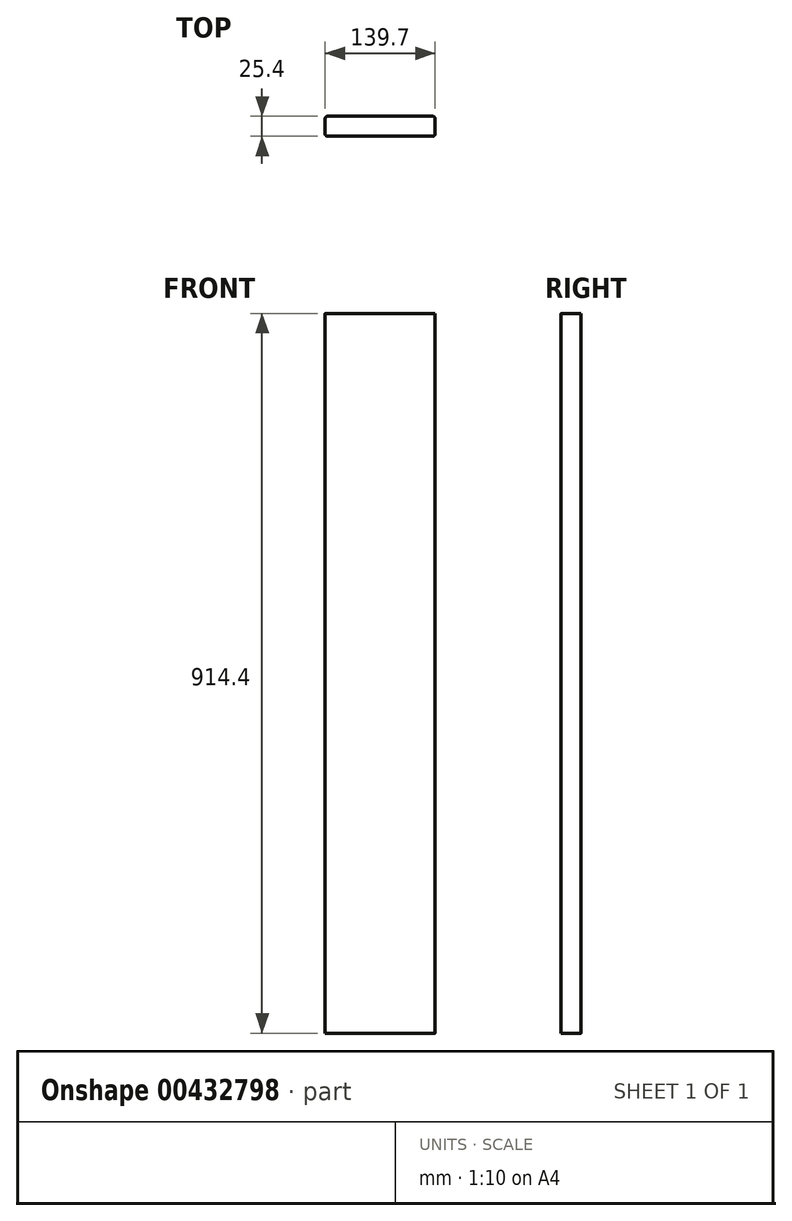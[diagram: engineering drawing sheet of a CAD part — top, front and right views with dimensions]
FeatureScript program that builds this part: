
annotation { "Feature Type Name" : "Feature", "Feature Type Description" : "" }
export const myFeature = defineFeature(function(context is Context, id is Id, definition is map)
    precondition{}
    {
        {
            assignVariable(context, id + "F0", {"name" : "Length", "anyValue" : 914.4 * mm});
        }
        {
            var Q0;
            Q0=qCreatedBy(makeId("Top.planeOp"),FACE);
            var sketch = newSketch(context, id + "F1", { "sketchPlane" : qUnion([Q0])});
            skLineSegment(sketch, "E0.bottom", {"start": v(66.68, -12.7) * mm, "end": v(-66.68, -12.7) * mm});
            skLineSegment(sketch, "E0.top", {"start": v(66.68, 12.7) * mm, "end": v(-66.68, 12.7) * mm});
            skLineSegment(sketch, "E0.left", {"start": v(69.85, -9.52) * mm, "end": v(69.85, 9.53) * mm});
            skLineSegment(sketch, "E0.right", {"start": v(-69.85, -9.53) * mm, "end": v(-69.85, 9.52) * mm});
            skPoint(sketch, "E0.middle", {"position": v(0, 0) * mm});
            skPoint(sketch, "E1.visualSharp", {"position": v(-69.85, 12.7) * mm});
            skArc(sketch, "E1.filletArc", {"start": v(-66.68, 12.7) * mm, "mid": v(-68.92, 11.77) * mm, "end": v(-69.85, 9.52) * mm});
            skPoint(sketch, "E2.visualSharp", {"position": v(-69.85, -12.7) * mm});
            skArc(sketch, "E2.filletArc", {"start": v(-69.85, -9.53) * mm, "mid": v(-68.92, -11.77) * mm, "end": v(-66.68, -12.7) * mm});
            skPoint(sketch, "E3.visualSharp", {"position": v(69.85, -12.7) * mm});
            skArc(sketch, "E3.filletArc", {"start": v(66.68, -12.7) * mm, "mid": v(68.92, -11.77) * mm, "end": v(69.85, -9.52) * mm});
            skPoint(sketch, "E4.visualSharp", {"position": v(69.85, 12.7) * mm});
            skArc(sketch, "E4.filletArc", {"start": v(69.85, 9.53) * mm, "mid": v(68.92, 11.77) * mm, "end": v(66.68, 12.7) * mm});
            skSolve(sketch);
        }
        {
            var Q0;
            Q0 = qSketchRegion(id + "F1", true);
            extrude(context, id + "F2", {"entities" : qUnion([Q0]), "oppositeDirection" : true, "offsetDistance" : 25.4 * mm, "depth" : getVariable(context, 'Length')});
        }
    });
